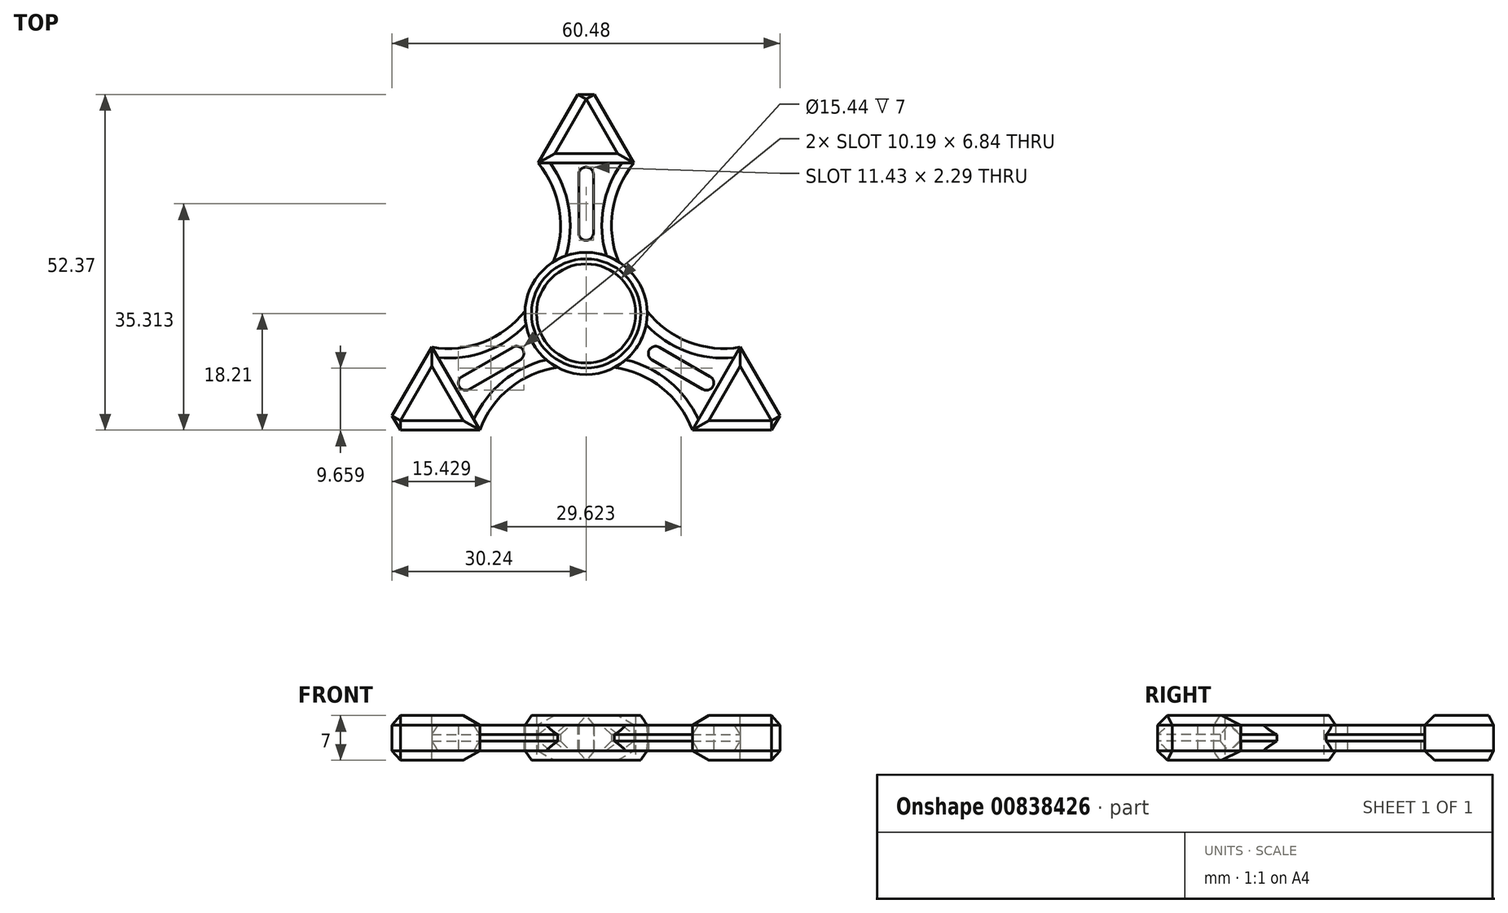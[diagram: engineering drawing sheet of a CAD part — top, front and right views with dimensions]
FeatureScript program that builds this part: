
annotation { "Feature Type Name" : "Feature", "Feature Type Description" : "" }
export const myFeature = defineFeature(function(context is Context, id is Id, definition is map)
    precondition{}
    {
        {
            var Q0;
            Q0=qCreatedBy(makeId("Top.planeOp"),FACE);
            var sketch = newSketch(context, id + "F0", { "sketchPlane" : qUnion([Q0])});
            skCircle(sketch, "E0", {"center": v(0, 0) * mm, "radius": 7.72 * mm});
            skCircle(sketch, "E1", {"center": v(0, 0) * mm, "radius": 9.52 * mm});
            skLineSegment(sketch, "E2", {"start": v(0, 36.41) * mm, "end": v(7.48, 23.45) * mm});
            skLineSegment(sketch, "E3", {"start": v(0, 36.41) * mm, "end": v(-7.48, 23.45) * mm});
            skLineSegment(sketch, "E4", {"start": v(-7.48, 23.45) * mm, "end": v(7.48, 23.45) * mm});
            skLineSegment(sketch, "E5.MirrorCS", {"start": v(16.57, -18.2) * mm, "end": v(24.05, -5.25) * mm});
            skLineSegment(sketch, "E6.MirrorCS", {"start": v(31.53, -18.2) * mm, "end": v(16.57, -18.2) * mm});
            skLineSegment(sketch, "E7.MirrorCS", {"start": v(31.53, -18.2) * mm, "end": v(24.05, -5.25) * mm});
            skLineSegment(sketch, "E8.MirrorCS", {"start": v(-16.57, -18.2) * mm, "end": v(-24.05, -5.25) * mm});
            skLineSegment(sketch, "E9.MirrorCS", {"start": v(-31.53, -18.2) * mm, "end": v(-24.05, -5.25) * mm});
            skLineSegment(sketch, "E10.MirrorCS", {"start": v(-31.53, -18.2) * mm, "end": v(-16.57, -18.2) * mm});
            skArc(sketch, "E11", {"start": v(7.48, 23.45) * mm, "mid": v(4.14, 16.08) * mm, "end": v(5.1, 8.05) * mm});
            skArc(sketch, "E12.MirrorCS", {"start": v(-7.48, 23.45) * mm, "mid": v(-4.14, 16.08) * mm, "end": v(-5.1, 8.05) * mm});
            skArc(sketch, "E13.MirrorCS", {"start": v(-16.57, -18.2) * mm, "mid": v(-11.86, -11.63) * mm, "end": v(-4.42, -8.43) * mm});
            skArc(sketch, "E14.MirrorCS", {"start": v(-24.05, -5.25) * mm, "mid": v(-16, -4.46) * mm, "end": v(-9.52, 0.39) * mm});
            skArc(sketch, "E15.MirrorCS", {"start": v(24.05, -5.25) * mm, "mid": v(16, -4.46) * mm, "end": v(9.52, 0.39) * mm});
            skArc(sketch, "E16.MirrorCS", {"start": v(16.57, -18.2) * mm, "mid": v(11.86, -11.63) * mm, "end": v(4.42, -8.43) * mm});
            skArc(sketch, "E17.0.startCap", {"start": v(-1.14, 21.68) * mm, "mid": v(0, 22.82) * mm, "end": v(1.14, 21.68) * mm});
            skArc(sketch, "E17.0.endCap", {"start": v(1.14, 12.53) * mm, "mid": v(0, 11.39) * mm, "end": v(-1.14, 12.53) * mm});
            skLineSegment(sketch, "E17.0.left", {"start": v(1.14, 21.68) * mm, "end": v(1.14, 12.53) * mm});
            skLineSegment(sketch, "E17.0.right", {"start": v(-1.14, 21.68) * mm, "end": v(-1.14, 12.53) * mm});
            skLineSegment(sketch, "E18.MirrorCS", {"start": v(18.2, -11.83) * mm, "end": v(10.28, -7.25) * mm});
            skLineSegment(sketch, "E19.MirrorCS", {"start": v(19.34, -9.85) * mm, "end": v(11.42, -5.27) * mm});
            skArc(sketch, "E20.MirrorCS", {"start": v(18.2, -11.83) * mm, "mid": v(19.76, -11.4) * mm, "end": v(19.34, -9.85) * mm});
            skArc(sketch, "E21.MirrorCS", {"start": v(11.42, -5.27) * mm, "mid": v(9.86, -5.7) * mm, "end": v(10.28, -7.25) * mm});
            skLineSegment(sketch, "E22.MirrorCS", {"start": v(-18.2, -11.83) * mm, "end": v(-10.28, -7.25) * mm});
            skLineSegment(sketch, "E23.MirrorCS", {"start": v(-19.34, -9.85) * mm, "end": v(-11.42, -5.27) * mm});
            skArc(sketch, "E24.MirrorCS", {"start": v(-11.42, -5.27) * mm, "mid": v(-9.86, -5.7) * mm, "end": v(-10.28, -7.25) * mm});
            skArc(sketch, "E25.MirrorCS", {"start": v(-18.2, -11.83) * mm, "mid": v(-19.76, -11.4) * mm, "end": v(-19.34, -9.85) * mm});
            skSolve(sketch);
        }
        {
            var Q0;
            Q0=makeQuery(id+"F0.imprint","IMPRINT",FACE,{"disambiguationData":[TD([[makeQuery(id+"F0.imprint","IMPRINT",EDGE,{"derivedFrom":sQuery(id+"F0.wireOp",EDGE,"E5.MirrorCS")}),-1.0]])]});
            var Q1;
            Q1=makeQuery(id+"F0.imprint","IMPRINT",FACE,{"disambiguationData":[TD([[makeQuery(id+"F0.imprint","IMPRINT",EDGE,{"derivedFrom":sQuery(id+"F0.wireOp",EDGE,"E0")}),-1.0]])]});
            var Q2;
            Q2=makeQuery(id+"F0.imprint","IMPRINT",FACE,{"disambiguationData":[TD([[makeQuery(id+"F0.imprint","IMPRINT",EDGE,{"derivedFrom":sQuery(id+"F0.wireOp",EDGE,"E2")}),-1.0]])]});
            var Q3;
            Q3=makeQuery(id+"F0.imprint","IMPRINT",FACE,{"disambiguationData":[TD([[makeQuery(id+"F0.imprint","IMPRINT",EDGE,{"derivedFrom":sQuery(id+"F0.wireOp",EDGE,"E8.MirrorCS")}),1.0]])]});
            extrude(context, id + "F1", {"entities" : qUnion([Q0, Q1, Q2, Q3]), "depth" : 7 * mm, "offsetDistance" : 25.4 * mm});
        }
        {
            var Q0;
            Q0=makeQuery(id+"F0.imprint","IMPRINT",FACE,{"disambiguationData":[TD([[makeQuery(id+"F0.imprint","IMPRINT",EDGE,{"derivedFrom":sQuery(id+"F0.wireOp",EDGE,"E4")}),-1.0]])]});
            var Q1;
            Q1=makeQuery(id+"F0.imprint","IMPRINT",FACE,{"disambiguationData":[TD([[makeQuery(id+"F0.imprint","IMPRINT",EDGE,{"derivedFrom":sQuery(id+"F0.wireOp",EDGE,"E8.MirrorCS")}),-1.0]])]});
            var Q2;
            Q2=makeQuery(id+"F0.imprint","IMPRINT",FACE,{"disambiguationData":[TD([[makeQuery(id+"F0.imprint","IMPRINT",EDGE,{"derivedFrom":sQuery(id+"F0.wireOp",EDGE,"E5.MirrorCS")}),1.0]])]});
            extrude(context, id + "F2", {"entities" : qUnion([Q0, Q1, Q2]), "depth" : 4 * mm, "offsetDistance" : 25.4 * mm});
        }
        {
            var Q0;
            Q0=makeQuery(id+"F2.opExtrude","SWEPT_BODY",BODY,{"disambiguationData":[OSD([sQuery(id+"F0.wireOp",EDGE,"E1"),sQuery(id+"F0.wireOp",EDGE,"E8.MirrorCS"),sQuery(id+"F0.wireOp",EDGE,"E13.MirrorCS"),sQuery(id+"F0.wireOp",EDGE,"E14.MirrorCS"),sQuery(id+"F0.wireOp",EDGE,"E22.MirrorCS"),sQuery(id+"F0.wireOp",EDGE,"E23.MirrorCS"),sQuery(id+"F0.wireOp",EDGE,"E24.MirrorCS"),sQuery(id+"F0.wireOp",EDGE,"E25.MirrorCS")])]});
            var Q1;
            Q1=makeQuery(id+"F2.opExtrude","SWEPT_BODY",BODY,{"disambiguationData":[OSD([sQuery(id+"F0.wireOp",EDGE,"E1"),sQuery(id+"F0.wireOp",EDGE,"E4"),sQuery(id+"F0.wireOp",EDGE,"E11"),sQuery(id+"F0.wireOp",EDGE,"E12.MirrorCS"),sQuery(id+"F0.wireOp",EDGE,"E17.0.startCap"),sQuery(id+"F0.wireOp",EDGE,"E17.0.endCap"),sQuery(id+"F0.wireOp",EDGE,"E17.0.left"),sQuery(id+"F0.wireOp",EDGE,"E17.0.right")])]});
            var Q2;
            Q2=makeQuery(id+"F2.opExtrude","SWEPT_BODY",BODY,{"disambiguationData":[OSD([sQuery(id+"F0.wireOp",EDGE,"E1"),sQuery(id+"F0.wireOp",EDGE,"E5.MirrorCS"),sQuery(id+"F0.wireOp",EDGE,"E15.MirrorCS"),sQuery(id+"F0.wireOp",EDGE,"E16.MirrorCS"),sQuery(id+"F0.wireOp",EDGE,"E18.MirrorCS"),sQuery(id+"F0.wireOp",EDGE,"E19.MirrorCS"),sQuery(id+"F0.wireOp",EDGE,"E20.MirrorCS"),sQuery(id+"F0.wireOp",EDGE,"E21.MirrorCS")])]});
            transform(context, id + "F3", {"entities" : qUnion([Q0, Q1, Q2]), "transformType" : TransformType.TRANSLATION_3D, "dx" : 0 * mm, "dy" : 0 * mm, "dz" : 1.5 * mm, "makeCopy" : false});
        }
        {
            var Q0;
            Q0=makeQuery(id+"F2.opExtrude","CAP_EDGE",EDGE,{"disambiguationData":[OSD([sQuery(id+"F0.wireOp",EDGE,"E16.MirrorCS")])],"isStart":false});
            var Q1;
            Q1=makeQuery(id+"F2.opExtrude","CAP_EDGE",EDGE,{"disambiguationData":[OSD([sQuery(id+"F0.wireOp",EDGE,"E16.MirrorCS")])],"isStart":true});
            var Q2;
            Q2=makeQuery(id+"F2.opExtrude","CAP_EDGE",EDGE,{"disambiguationData":[OSD([sQuery(id+"F0.wireOp",EDGE,"E15.MirrorCS")])],"isStart":false});
            var Q3;
            Q3=makeQuery(id+"F2.opExtrude","CAP_EDGE",EDGE,{"disambiguationData":[OSD([sQuery(id+"F0.wireOp",EDGE,"E15.MirrorCS")])],"isStart":true});
            var Q4;
            Q4=makeQuery(id+"F2.opExtrude","CAP_EDGE",EDGE,{"disambiguationData":[OSD([sQuery(id+"F0.wireOp",EDGE,"E11")])],"isStart":true});
            var Q5;
            Q5=makeQuery(id+"F2.opExtrude","CAP_EDGE",EDGE,{"disambiguationData":[OSD([sQuery(id+"F0.wireOp",EDGE,"E11")])],"isStart":false});
            var Q6;
            Q6=makeQuery(id+"F2.opExtrude","CAP_EDGE",EDGE,{"disambiguationData":[OSD([sQuery(id+"F0.wireOp",EDGE,"E12.MirrorCS")])],"isStart":false});
            var Q7;
            Q7=makeQuery(id+"F2.opExtrude","CAP_EDGE",EDGE,{"disambiguationData":[OSD([sQuery(id+"F0.wireOp",EDGE,"E12.MirrorCS")])],"isStart":true});
            var Q8;
            Q8=makeQuery(id+"F2.opExtrude","CAP_EDGE",EDGE,{"disambiguationData":[OSD([sQuery(id+"F0.wireOp",EDGE,"E14.MirrorCS")])],"isStart":true});
            var Q9;
            Q9=makeQuery(id+"F2.opExtrude","CAP_EDGE",EDGE,{"disambiguationData":[OSD([sQuery(id+"F0.wireOp",EDGE,"E14.MirrorCS")])],"isStart":false});
            var Q10;
            Q10=makeQuery(id+"F2.opExtrude","CAP_EDGE",EDGE,{"disambiguationData":[OSD([sQuery(id+"F0.wireOp",EDGE,"E13.MirrorCS")])],"isStart":false});
            var Q11;
            Q11=makeQuery(id+"F2.opExtrude","CAP_EDGE",EDGE,{"disambiguationData":[OSD([sQuery(id+"F0.wireOp",EDGE,"E13.MirrorCS")])],"isStart":true});
            var Q12;
            Q12=makeQuery(id+"F1.opExtrude","CAP_EDGE",EDGE,{"disambiguationData":[OSD([sQuery(id+"F0.wireOp",EDGE,"E4")])],"isStart":false});
            var Q13;
            Q13=makeQuery(id+"F1.opExtrude","CAP_EDGE",EDGE,{"disambiguationData":[OSD([sQuery(id+"F0.wireOp",EDGE,"E3")])],"isStart":false});
            var Q14;
            Q14=makeQuery(id+"F1.opExtrude","CAP_EDGE",EDGE,{"disambiguationData":[OSD([sQuery(id+"F0.wireOp",EDGE,"E2")])],"isStart":false});
            var Q15;
            Q15=makeQuery(id+"F1.opExtrude","SWEPT_EDGE",EDGE,{"disambiguationData":[OSD([sQuery(id+"F0.wireOp",EDGE,"E2"),sQuery(id+"F0.wireOp",EDGE,"E3")])]});
            var Q16;
            Q16=makeQuery(id+"F1.opExtrude","CAP_EDGE",EDGE,{"disambiguationData":[OSD([sQuery(id+"F0.wireOp",EDGE,"E2")])],"isStart":true});
            var Q17;
            Q17=makeQuery(id+"F1.opExtrude","CAP_EDGE",EDGE,{"disambiguationData":[OSD([sQuery(id+"F0.wireOp",EDGE,"E3")])],"isStart":true});
            var Q18;
            Q18=makeQuery(id+"F1.opExtrude","CAP_EDGE",EDGE,{"disambiguationData":[OSD([sQuery(id+"F0.wireOp",EDGE,"E6.MirrorCS")])],"isStart":false});
            var Q19;
            Q19=makeQuery(id+"F1.opExtrude","CAP_EDGE",EDGE,{"disambiguationData":[OSD([sQuery(id+"F0.wireOp",EDGE,"E6.MirrorCS")])],"isStart":true});
            var Q20;
            Q20=makeQuery(id+"F1.opExtrude","SWEPT_EDGE",EDGE,{"disambiguationData":[OSD([sQuery(id+"F0.wireOp",EDGE,"E6.MirrorCS"),sQuery(id+"F0.wireOp",EDGE,"E7.MirrorCS")])]});
            var Q21;
            Q21=makeQuery(id+"F1.opExtrude","CAP_EDGE",EDGE,{"disambiguationData":[OSD([sQuery(id+"F0.wireOp",EDGE,"E7.MirrorCS")])],"isStart":false});
            var Q22;
            Q22=makeQuery(id+"F1.opExtrude","CAP_EDGE",EDGE,{"disambiguationData":[OSD([sQuery(id+"F0.wireOp",EDGE,"E7.MirrorCS")])],"isStart":true});
            var Q23;
            Q23=makeQuery(id+"F1.opExtrude","SWEPT_EDGE",EDGE,{"disambiguationData":[OSD([sQuery(id+"F0.wireOp",EDGE,"E9.MirrorCS"),sQuery(id+"F0.wireOp",EDGE,"E10.MirrorCS")])]});
            var Q24;
            Q24=makeQuery(id+"F1.opExtrude","CAP_EDGE",EDGE,{"disambiguationData":[OSD([sQuery(id+"F0.wireOp",EDGE,"E10.MirrorCS")])],"isStart":true});
            var Q25;
            Q25=makeQuery(id+"F1.opExtrude","CAP_EDGE",EDGE,{"disambiguationData":[OSD([sQuery(id+"F0.wireOp",EDGE,"E9.MirrorCS")])],"isStart":true});
            var Q26;
            Q26=makeQuery(id+"F1.opExtrude","CAP_EDGE",EDGE,{"disambiguationData":[OSD([sQuery(id+"F0.wireOp",EDGE,"E9.MirrorCS")])],"isStart":false});
            var Q27;
            Q27=makeQuery(id+"F1.opExtrude","CAP_EDGE",EDGE,{"disambiguationData":[OSD([sQuery(id+"F0.wireOp",EDGE,"E10.MirrorCS")])],"isStart":false});
            var Q28;
            Q28=makeQuery(id+"F1.opExtrude","CAP_EDGE",EDGE,{"disambiguationData":[OSD([sQuery(id+"F0.wireOp",EDGE,"E8.MirrorCS")])],"isStart":false});
            var Q29;
            Q29=makeQuery(id+"F1.opExtrude","CAP_EDGE",EDGE,{"disambiguationData":[OSD([sQuery(id+"F0.wireOp",EDGE,"E5.MirrorCS")])],"isStart":false});
            var Q30;
            Q30=makeQuery(id+"F1.opExtrude","CAP_EDGE",EDGE,{"disambiguationData":[OSD([sQuery(id+"F0.wireOp",EDGE,"E5.MirrorCS")])],"isStart":true});
            var Q31;
            Q31=makeQuery(id+"F1.opExtrude","CAP_EDGE",EDGE,{"disambiguationData":[OSD([sQuery(id+"F0.wireOp",EDGE,"E4")])],"isStart":true});
            var Q32;
            Q32=makeQuery(id+"F1.opExtrude","CAP_EDGE",EDGE,{"disambiguationData":[OSD([sQuery(id+"F0.wireOp",EDGE,"E8.MirrorCS")])],"isStart":true});
            chamfer(context, id + "F4", {"entities" : qUnion([Q0, Q1, Q2, Q3, Q4, Q5, Q6, Q7, Q8, Q9, Q10, Q11, Q12, Q13, Q14, Q15, Q16, Q17, Q18, Q19, Q20, Q21, Q22, Q23, Q24, Q25, Q26, Q27, Q28, Q29, Q30, Q31, Q32]), "width" : 1.5 * mm, "tangentPropagation" : true});
        }
        {
            var Q0;
            Q0=makeQuery(id+"F1.opExtrude","CAP_EDGE",EDGE,{"disambiguationData":[OSD([sQuery(id+"F0.wireOp",EDGE,"E1")])],"isStart":false});
            var Q1;
            Q1=makeQuery(id+"F1.opExtrude","CAP_EDGE",EDGE,{"disambiguationData":[OSD([sQuery(id+"F0.wireOp",EDGE,"E1")])],"isStart":true});
            chamfer(context, id + "F5", {"entities" : qUnion([Q0, Q1]), "chamferType" : ChamferType.TWO_OFFSETS, "width1" : 1.02 * mm, "oppositeDirection" : false, "width2" : 1.5 * mm, "tangentPropagation" : true});
        }
    });
